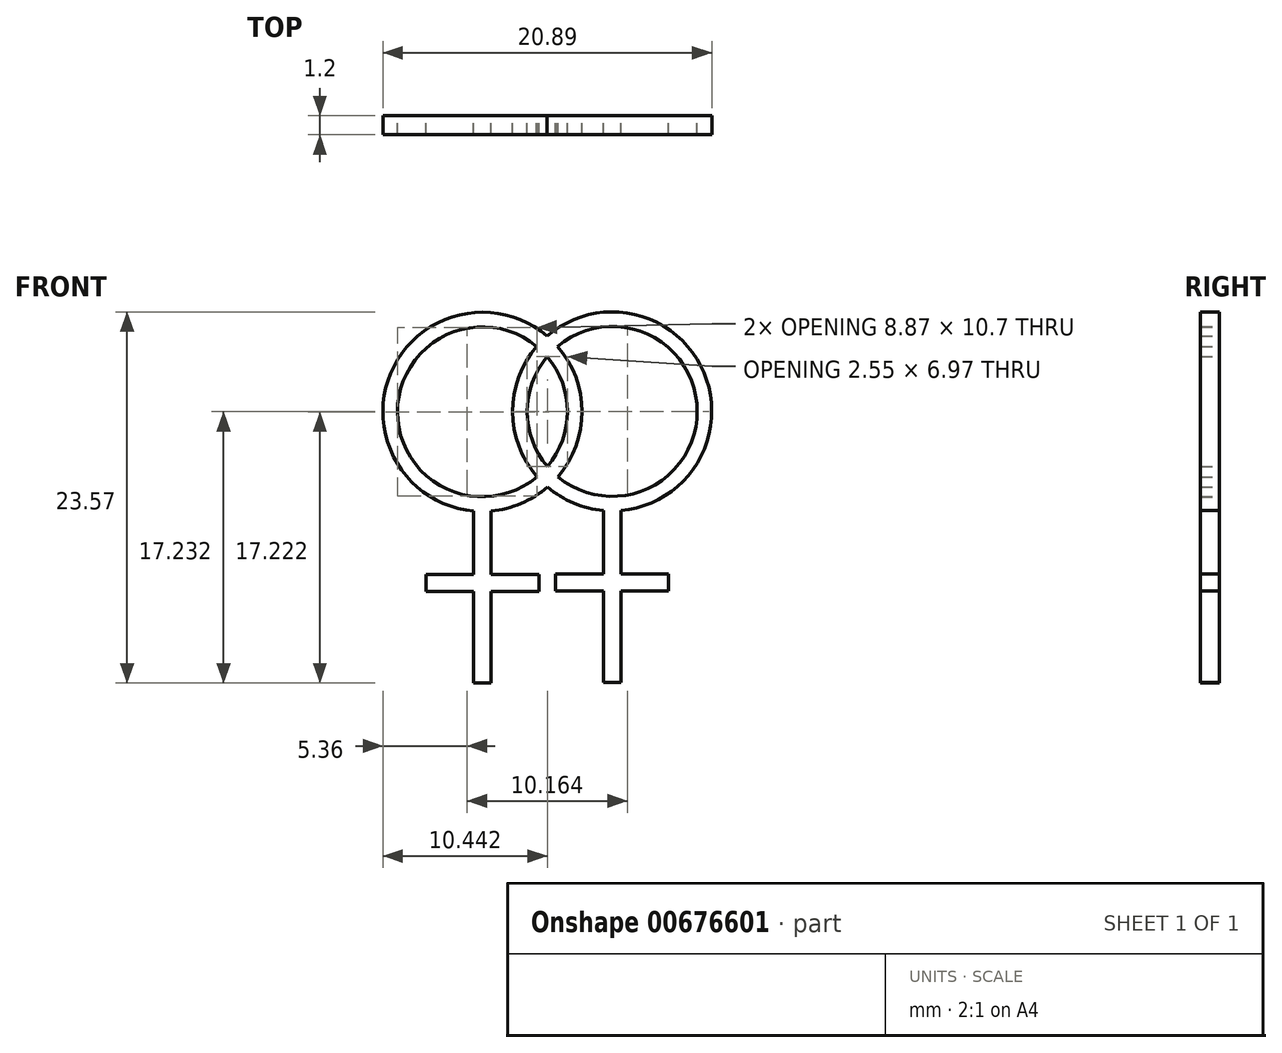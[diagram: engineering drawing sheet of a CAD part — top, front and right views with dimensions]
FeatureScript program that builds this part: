
annotation { "Feature Type Name" : "Feature", "Feature Type Description" : "" }
export const myFeature = defineFeature(function(context is Context, id is Id, definition is map)
    precondition{}
    {
        {
            var Q0;
            Q0=qCreatedBy(makeId("Front.planeOp"),FACE);
            var sketch = newSketch(context, id + "F0", { "sketchPlane" : qUnion([Q0])});
            skArc(sketch, "E0", {"start": v(-22.56, 17.55) * mm, "mid": v(-20.65, 18.03) * mm, "end": v(-18.97, 19.07) * mm});
            skArc(sketch, "E1", {"start": v(-19.66, 28) * mm, "mid": v(-28.5, 23.83) * mm, "end": v(-19.63, 19.72) * mm});
            skLineSegment(sketch, "E2", {"start": v(-23.66, 12.43) * mm, "end": v(-23.66, 6.63) * mm});
            skLineSegment(sketch, "E3", {"start": v(-22.56, 12.43) * mm, "end": v(-22.56, 6.63) * mm});
            skLineSegment(sketch, "E4", {"start": v(-23.66, 6.63) * mm, "end": v(-22.56, 6.63) * mm});
            skPoint(sketch, "E5.orphan", {"position": v(-22.91, 6.63) * mm});
            skPoint(sketch, "E6.start.orphan", {"position": v(-23.1, 30.17) * mm});
            skPoint(sketch, "E7.oppositeSnap0", {"position": v(-22.56, 12.43) * mm});
            skPoint(sketch, "E7.right.end.orphan", {"position": v(-17.65, 12.43) * mm});
            skLineSegment(sketch, "E8", {"start": v(-23.66, 17.55) * mm, "end": v(-23.66, 13.53) * mm});
            skLineSegment(sketch, "E9", {"start": v(-23.66, 13.53) * mm, "end": v(-26.7, 13.53) * mm});
            skLineSegment(sketch, "E10", {"start": v(-26.7, 13.53) * mm, "end": v(-26.7, 12.43) * mm});
            skLineSegment(sketch, "E11", {"start": v(-26.7, 12.43) * mm, "end": v(-23.66, 12.43) * mm});
            skLineSegment(sketch, "E12", {"start": v(-22.56, 17.55) * mm, "end": v(-22.56, 13.53) * mm});
            skLineSegment(sketch, "E13", {"start": v(-22.56, 13.53) * mm, "end": v(-19.52, 13.53) * mm});
            skLineSegment(sketch, "E14", {"start": v(-19.52, 13.53) * mm, "end": v(-19.52, 12.43) * mm});
            skLineSegment(sketch, "E15", {"start": v(-19.52, 12.43) * mm, "end": v(-22.56, 12.43) * mm});
            skArc(sketch, "E16", {"start": v(-14.32, 17.58) * mm, "mid": v(-9.04, 26.34) * mm, "end": v(-19, 28.66) * mm});
            skArc(sketch, "E17", {"start": v(-19, 27.35) * mm, "mid": v(-20.26, 23.86) * mm, "end": v(-18.98, 20.38) * mm});
            skLineSegment(sketch, "E18", {"start": v(-15.42, 12.46) * mm, "end": v(-15.42, 6.66) * mm});
            skLineSegment(sketch, "E19", {"start": v(-14.32, 12.46) * mm, "end": v(-14.32, 6.66) * mm});
            skLineSegment(sketch, "E20", {"start": v(-15.42, 6.66) * mm, "end": v(-14.32, 6.66) * mm});
            skPoint(sketch, "E21.orphan", {"position": v(-14.67, 6.66) * mm});
            skPoint(sketch, "E22.start.orphan", {"position": v(-14.87, 30.2) * mm});
            skPoint(sketch, "E23.oppositeSnap0", {"position": v(-14.32, 12.46) * mm});
            skPoint(sketch, "E23.right.end.orphan", {"position": v(-9.41, 12.46) * mm});
            skLineSegment(sketch, "E24", {"start": v(-15.42, 17.58) * mm, "end": v(-15.42, 13.56) * mm});
            skLineSegment(sketch, "E25", {"start": v(-15.42, 13.56) * mm, "end": v(-18.46, 13.56) * mm});
            skLineSegment(sketch, "E26", {"start": v(-18.46, 13.56) * mm, "end": v(-18.46, 12.46) * mm});
            skLineSegment(sketch, "E27", {"start": v(-18.46, 12.46) * mm, "end": v(-15.42, 12.46) * mm});
            skLineSegment(sketch, "E28", {"start": v(-14.32, 17.58) * mm, "end": v(-14.32, 13.56) * mm});
            skLineSegment(sketch, "E29", {"start": v(-14.32, 13.56) * mm, "end": v(-11.28, 13.56) * mm});
            skLineSegment(sketch, "E30", {"start": v(-11.28, 13.56) * mm, "end": v(-11.28, 12.46) * mm});
            skLineSegment(sketch, "E31", {"start": v(-11.28, 12.46) * mm, "end": v(-14.32, 12.46) * mm});
            skArc(sketch, "E32.trimOffspring", {"start": v(-19, 28.66) * mm, "mid": v(-28.94, 26.3) * mm, "end": v(-23.66, 17.55) * mm});
            skArc(sketch, "E33.trimOffspring", {"start": v(-19.66, 28) * mm, "mid": v(-21.2, 23.86) * mm, "end": v(-19.63, 19.72) * mm});
            skArc(sketch, "E34.trimOffspring", {"start": v(-18.32, 19.72) * mm, "mid": v(-9.47, 23.9) * mm, "end": v(-18.34, 28) * mm});
            skArc(sketch, "E35.trimOffspring", {"start": v(-18.32, 19.72) * mm, "mid": v(-16.79, 23.87) * mm, "end": v(-18.34, 28) * mm});
            skArc(sketch, "E36.trimOffspring", {"start": v(-18.98, 20.38) * mm, "mid": v(-17.71, 23.87) * mm, "end": v(-19, 27.35) * mm});
            skArc(sketch, "E37.trimOffspring", {"start": v(-18.97, 19.07) * mm, "mid": v(-17.31, 18.04) * mm, "end": v(-15.42, 17.58) * mm});
            skSolve(sketch);
        }
        {
            var Q0;
            Q0=makeQuery(id+"F0.imprint","IMPRINT",FACE,{"disambiguationData":[TD([[makeQuery(id+"F0.imprint","IMPRINT",EDGE,{"derivedFrom":sQuery(id+"F0.wireOp",EDGE,"E0")}),1.0]])]});
            extrude(context, id + "F1", {"entities" : qUnion([Q0]), "depth" : 1.2 * mm, "offsetDistance" : 25.4 * mm});
        }
    });
